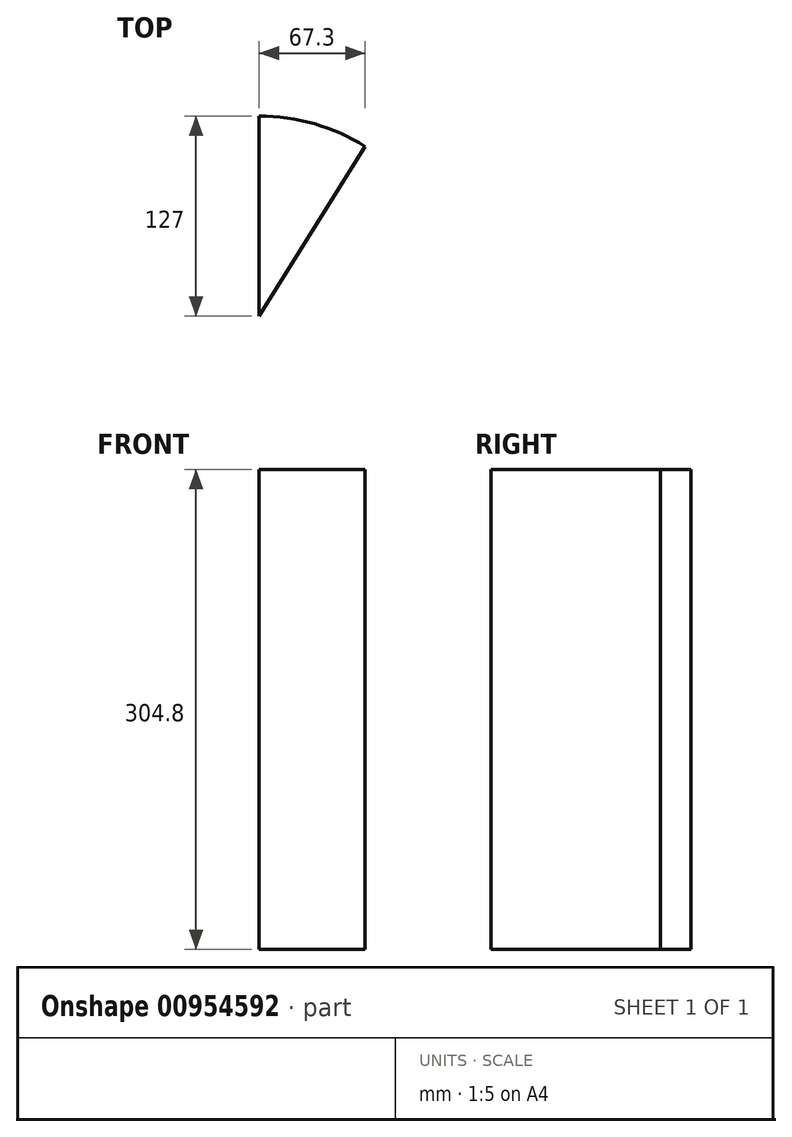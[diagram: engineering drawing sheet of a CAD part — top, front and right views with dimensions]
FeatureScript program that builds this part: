
annotation { "Feature Type Name" : "Feature", "Feature Type Description" : "" }
export const myFeature = defineFeature(function(context is Context, id is Id, definition is map)
    precondition{}
    {
        {
            var Q0;
            Q0=qCreatedBy(makeId("Top.planeOp"),FACE);
            var sketch = newSketch(context, id + "F0", { "sketchPlane" : qUnion([Q0])});
            skCircle(sketch, "E0", {"center": v(0, 0) * mm, "radius": 127 * mm});
            skSolve(sketch);
        }
        {
            var Q0;
            Q0=qCreatedBy(makeId("Top.planeOp"),FACE);
            var sketch = newSketch(context, id + "F1", { "sketchPlane" : qUnion([Q0])});
            skLineSegment(sketch, "E1", {"start": v(0, 0) * mm, "end": v(0, 127) * mm});
            skLineSegment(sketch, "E2", {"start": v(67.3, 107.7) * mm, "end": v(0, 0) * mm});
            skArc(sketch, "E3.0", {"start": v(67.3, 107.7) * mm, "mid": v(35, 122.08) * mm, "end": v(0, 127) * mm});
            skSolve(sketch);
        }
        {
            var Q0;
            Q0=makeQuery(id+"F1.imprint","IMPRINT",FACE,{"disambiguationData":[TD([[makeQuery(id+"F1.imprint","IMPRINT",EDGE,{"derivedFrom":sQuery(id+"F1.wireOp",EDGE,"E1")}),-1.0]])]});
            extrude(context, id + "F2", {"entities" : qUnion([Q0]), "depth" : 304.8 * mm, "offsetDistance" : 25.4 * mm});
        }
    });
